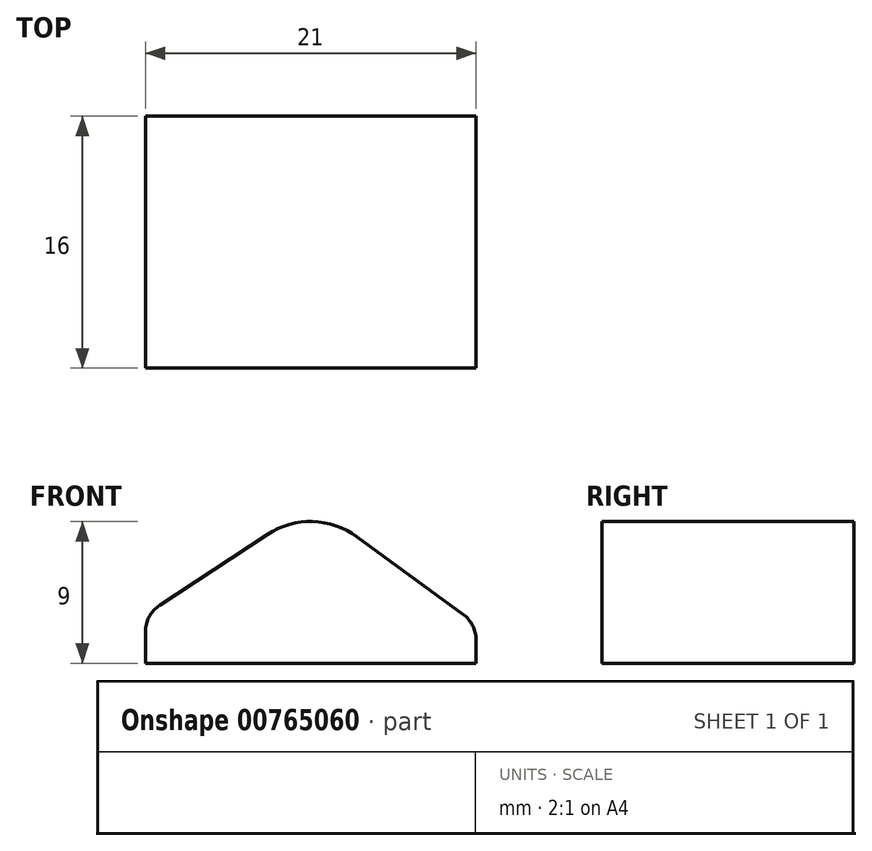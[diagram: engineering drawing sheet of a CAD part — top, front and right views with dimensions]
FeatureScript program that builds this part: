
annotation { "Feature Type Name" : "Feature", "Feature Type Description" : "" }
export const myFeature = defineFeature(function(context is Context, id is Id, definition is map)
    precondition{}
    {
        {
            var Q0;
            Q0=qCreatedBy(makeId("Front.planeOp"),FACE);
            var sketch = newSketch(context, id + "F0", { "sketchPlane" : qUnion([Q0])});
            skLineSegment(sketch, "E0", {"start": v(-35.09, 8.8) * mm, "end": v(-14.09, 8.8) * mm});
            skArc(sketch, "E1", {"start": v(-21.63, 16.84) * mm, "mid": v(-24.46, 17.8) * mm, "end": v(-27.33, 16.98) * mm});
            skArc(sketch, "E2", {"start": v(-14.09, 10.3) * mm, "mid": v(-14.3, 11.2) * mm, "end": v(-14.9, 11.91) * mm});
            skArc(sketch, "E3", {"start": v(-34.19, 12.47) * mm, "mid": v(-34.85, 11.75) * mm, "end": v(-35.09, 10.8) * mm});
            skLineSegment(sketch, "E4", {"start": v(-21.63, 16.84) * mm, "end": v(-14.9, 11.91) * mm});
            skLineSegment(sketch, "E5", {"start": v(-35.09, 8.8) * mm, "end": v(-35.09, 10.8) * mm});
            skLineSegment(sketch, "E6", {"start": v(-14.09, 8.8) * mm, "end": v(-14.09, 10.3) * mm});
            skLineSegment(sketch, "E7", {"start": v(-34.19, 12.47) * mm, "end": v(-27.33, 16.98) * mm});
            skSolve(sketch);
        }
        {
            var Q0;
            Q0=makeQuery(id+"F0.imprint","IMPRINT",FACE,{"disambiguationData":[TD([[makeQuery(id+"F0.imprint","IMPRINT",EDGE,{"derivedFrom":sQuery(id+"F0.wireOp",EDGE,"E0")}),1.0]])]});
            extrude(context, id + "F1", {"entities" : qUnion([Q0]), "depth" : 16 * mm, "offsetDistance" : 25 * mm});
        }
    });
